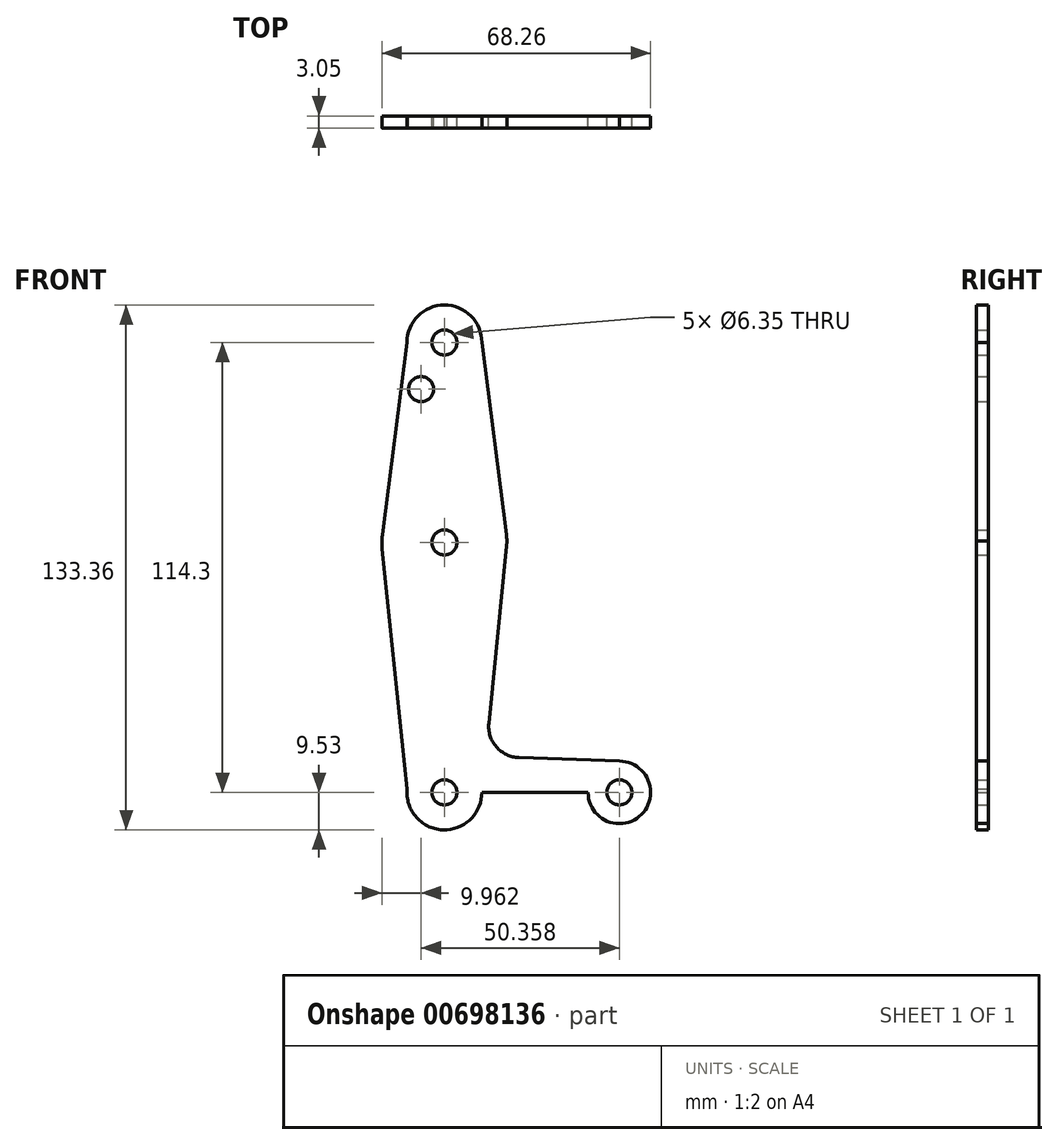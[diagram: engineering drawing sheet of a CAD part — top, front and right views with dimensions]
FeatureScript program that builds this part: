
annotation { "Feature Type Name" : "Feature", "Feature Type Description" : "" }
export const myFeature = defineFeature(function(context is Context, id is Id, definition is map)
    precondition{}
    {
        {
            var Q0;
            Q0=qCreatedBy(makeId("Front.planeOp"),FACE);
            var sketch = newSketch(context, id + "F0", { "sketchPlane" : qUnion([Q0])});
            skLineSegment(sketch, "E0", {"start": v(0, 0) * mm, "end": v(0, 114.3) * mm});
            skCircle(sketch, "E1", {"center": v(0, 114.3) * mm, "radius": 9.53 * mm});
            skCircle(sketch, "E2", {"center": v(0, 0) * mm, "radius": 9.53 * mm});
            skCircle(sketch, "E3", {"center": v(0, 63.5) * mm, "radius": 15.88 * mm});
            skLineSegment(sketch, "E4", {"start": v(0, 0) * mm, "end": v(44.45, 0) * mm});
            skCircle(sketch, "E5", {"center": v(44.45, 0) * mm, "radius": 7.94 * mm});
            skLineSegment(sketch, "E6", {"start": v(-9.53, 114.3) * mm, "end": v(-15.75, 65.5) * mm});
            skLineSegment(sketch, "E7", {"start": v(9.53, 114.3) * mm, "end": v(15.75, 65.5) * mm});
            skLineSegment(sketch, "E8", {"start": v(15.87, 63.83) * mm, "end": v(11.27, 17.58) * mm});
            skLineSegment(sketch, "E9", {"start": v(-15.8, 61.87) * mm, "end": v(-9.48, 0.91) * mm});
            skLineSegment(sketch, "E10", {"start": v(0, -9.53) * mm, "end": v(44.73, -7.93) * mm});
            skLineSegment(sketch, "E11", {"start": v(18.9, 8.85) * mm, "end": v(44.45, 7.94) * mm});
            skCircle(sketch, "E12", {"center": v(0, 114.3) * mm, "radius": 3.18 * mm});
            skCircle(sketch, "E13", {"center": v(0, 63.5) * mm, "radius": 3.18 * mm});
            skCircle(sketch, "E14", {"center": v(0, 0) * mm, "radius": 3.18 * mm});
            skCircle(sketch, "E15", {"center": v(44.45, 0) * mm, "radius": 3.18 * mm});
            skArc(sketch, "E16.filletArc", {"start": v(11.27, 17.58) * mm, "mid": v(13.2, 11.56) * mm, "end": v(18.9, 8.85) * mm});
            skCircle(sketch, "E17", {"center": v(-5.9, 102.44) * mm, "radius": 3.18 * mm});
            skSolve(sketch);
        }
        {
            var Q0;
            {var subQ0=sQuery(id+"F0.wireOp",EDGE,"E6");Q0=makeQuery(id+"F0.imprint","IMPRINT",FACE,{"disambiguationData":[TD([[makeQuery(id+"F0.imprint","IMPRINT",EDGE,{"derivedFrom":subQ0}),1.0]])]});}
            var Q1;
            {var subQ5=sQuery(id+"F0.wireOp",EDGE,"E7");Q1=makeQuery(id+"F0.imprint","IMPRINT",FACE,{"disambiguationData":[TD([[makeQuery(id+"F0.imprint","IMPRINT",EDGE,{"derivedFrom":subQ5}),-1.0]])]});}
            var Q2;
            Q2=makeQuery(id+"F0.imprint","IMPRINT",FACE,{"disambiguationData":[TD([[makeQuery(id+"F0.imprint","IMPRINT",EDGE,{"derivedFrom":sQuery(id+"F0.wireOp",EDGE,"E12")}),-1.0]])]});
            var Q3;
            {var subQ0=sQuery(id+"F0.wireOp",EDGE,"E3");var subQ2=sQuery(id+"F0.wireOp",EDGE,"E0");var subQ7=makeQuery(id+"F0.imprint","INTERSECT",VERTEX,{"disambiguationData":[OD(0.0)],"derivedFrom":[subQ2,subQ0]});Q3=makeQuery(id+"F0.imprint","IMPRINT",FACE,{"disambiguationData":[TD([[makeQuery(id+"F0.imprint","IMPRINT",EDGE,{"disambiguationData":[TD([[subQ7,-1.0]])],"derivedFrom":subQ2}),1.0]])]});}
            var Q4;
            {var subQ0=sQuery(id+"F0.wireOp",EDGE,"E3");var subQ2=sQuery(id+"F0.wireOp",EDGE,"E0");var subQ9=makeQuery(id+"F0.imprint","INTERSECT",VERTEX,{"disambiguationData":[OD(0.0)],"derivedFrom":[subQ2,subQ0]});Q4=makeQuery(id+"F0.imprint","IMPRINT",FACE,{"disambiguationData":[TD([[makeQuery(id+"F0.imprint","IMPRINT",EDGE,{"disambiguationData":[TD([[subQ9,-1.0]])],"derivedFrom":subQ2}),-1.0]])]});}
            var Q5;
            {var subQ5=sQuery(id+"F0.wireOp",EDGE,"E9");Q5=makeQuery(id+"F0.imprint","IMPRINT",FACE,{"disambiguationData":[TD([[makeQuery(id+"F0.imprint","IMPRINT",EDGE,{"derivedFrom":subQ5}),1.0]])]});}
            var Q6;
            {var subQ0=sQuery(id+"F0.wireOp",EDGE,"E10");var subQ1=sQuery(id+"F0.wireOp",EDGE,"E2");var subQ2=makeQuery(id+"F0.imprint","INTERSECT",VERTEX,{"disambiguationData":[OD(1.0)],"derivedFrom":[subQ1,subQ0]});Q6=makeQuery(id+"F0.imprint","IMPRINT",FACE,{"disambiguationData":[TD([[makeQuery(id+"F0.imprint","IMPRINT",EDGE,{"disambiguationData":[TD([[subQ2,-1.0]])],"derivedFrom":subQ1}),-1.0]])]});}
            var Q7;
            {var subQ7=sQuery(id+"F0.wireOp",EDGE,"E14");var subQ8=sQuery(id+"F0.wireOp",EDGE,"E0");var subQ9=makeQuery(id+"F0.imprint","INTERSECT",VERTEX,{"derivedFrom":[subQ8,subQ7]});Q7=makeQuery(id+"F0.imprint","IMPRINT",FACE,{"disambiguationData":[TD([[makeQuery(id+"F0.imprint","IMPRINT",EDGE,{"disambiguationData":[TD([[subQ9,-1.0]])],"derivedFrom":subQ8}),1.0]])]});}
            var Q8;
            {var subQ0=sQuery(id+"F0.wireOp",EDGE,"E14");var subQ1=sQuery(id+"F0.wireOp",EDGE,"E0");var subQ2=makeQuery(id+"F0.imprint","INTERSECT",VERTEX,{"derivedFrom":[subQ1,subQ0]});Q8=makeQuery(id+"F0.imprint","IMPRINT",FACE,{"disambiguationData":[TD([[makeQuery(id+"F0.imprint","IMPRINT",EDGE,{"disambiguationData":[TD([[subQ2,-1.0]])],"derivedFrom":subQ1}),-1.0]])]});}
            var Q9;
            Q9=makeQuery(id+"F0.imprint","IMPRINT",FACE,{"disambiguationData":[TD([[makeQuery(id+"F0.imprint","IMPRINT",EDGE,{"derivedFrom":sQuery(id+"F0.wireOp",EDGE,"E15")}),-1.0]])]});
            var Q10;
            {var subQ9=sQuery(id+"F0.wireOp",EDGE,"E11");Q10=makeQuery(id+"F0.imprint","IMPRINT",FACE,{"disambiguationData":[TD([[makeQuery(id+"F0.imprint","IMPRINT",EDGE,{"derivedFrom":subQ9}),-1.0]])]});}
            extrude(context, id + "F1", {"entities" : qUnion([Q0, Q1, Q2, Q3, Q4, Q5, Q6, Q7, Q8, Q9, Q10]), "depth" : 3.05 * mm, "offsetDistance" : 25.4 * mm});
        }
    });
